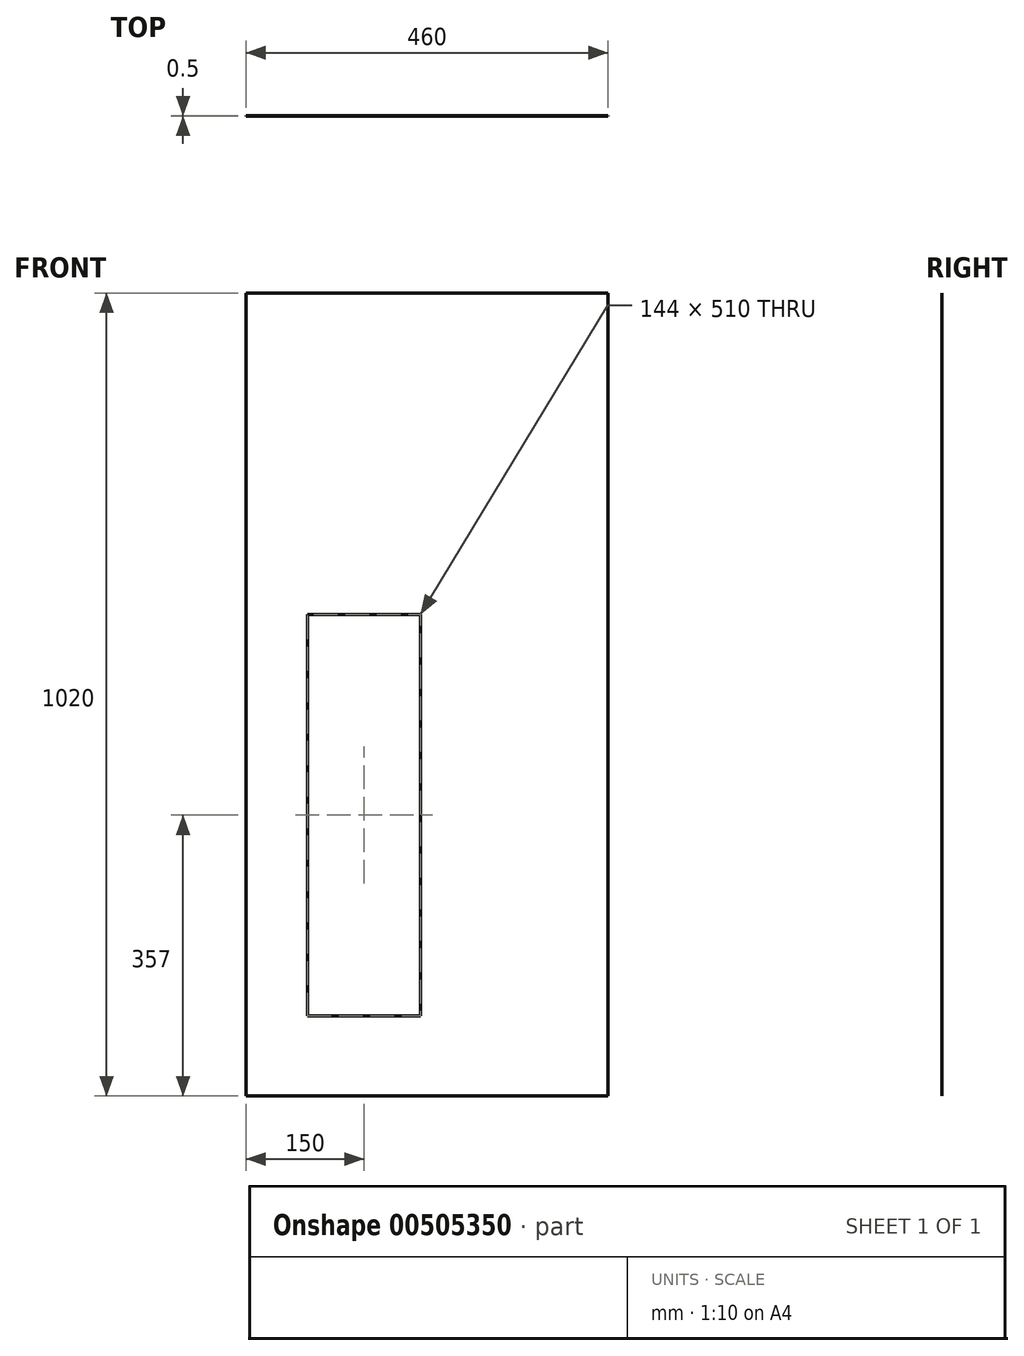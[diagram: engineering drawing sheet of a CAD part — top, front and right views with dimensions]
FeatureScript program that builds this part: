
annotation { "Feature Type Name" : "Feature", "Feature Type Description" : "" }
export const myFeature = defineFeature(function(context is Context, id is Id, definition is map)
    precondition{}
    {
        {
            var Q0;
            Q0=qCreatedBy(makeId("Front.planeOp"),FACE);
            var sketch = newSketch(context, id + "F0", { "sketchPlane" : qUnion([Q0])});
            skLineSegment(sketch, "E0.bottom", {"start": v(-230, 510) * mm, "end": v(230, 510) * mm});
            skLineSegment(sketch, "E0.top", {"start": v(-230, -510) * mm, "end": v(230, -510) * mm});
            skLineSegment(sketch, "E0.left", {"start": v(-230, 510) * mm, "end": v(-230, -510) * mm});
            skLineSegment(sketch, "E0.right", {"start": v(230, 510) * mm, "end": v(230, -510) * mm});
            skPoint(sketch, "E0.middle", {"position": v(0, 0) * mm});
            skLineSegment(sketch, "E1.bottom", {"start": v(-152, 102) * mm, "end": v(-8, 102) * mm});
            skLineSegment(sketch, "E1.top", {"start": v(-152, -408) * mm, "end": v(-8, -408) * mm});
            skLineSegment(sketch, "E1.left", {"start": v(-152, 102) * mm, "end": v(-152, -408) * mm});
            skLineSegment(sketch, "E1.right", {"start": v(-8, 102) * mm, "end": v(-8, -408) * mm});
            skSolve(sketch);
        }
        {
            var Q0;
            Q0=makeQuery(id+"F0.imprint","IMPRINT",FACE,{"disambiguationData":[TD([[makeQuery(id+"F0.imprint","IMPRINT",EDGE,{"derivedFrom":sQuery(id+"F0.wireOp",EDGE,"E0.bottom")}),-1.0]])]});
            extrude(context, id + "F1", {"entities" : qUnion([Q0]), "depth" : 0.5 * mm, "offsetDistance" : 25 * mm});
        }
    });
